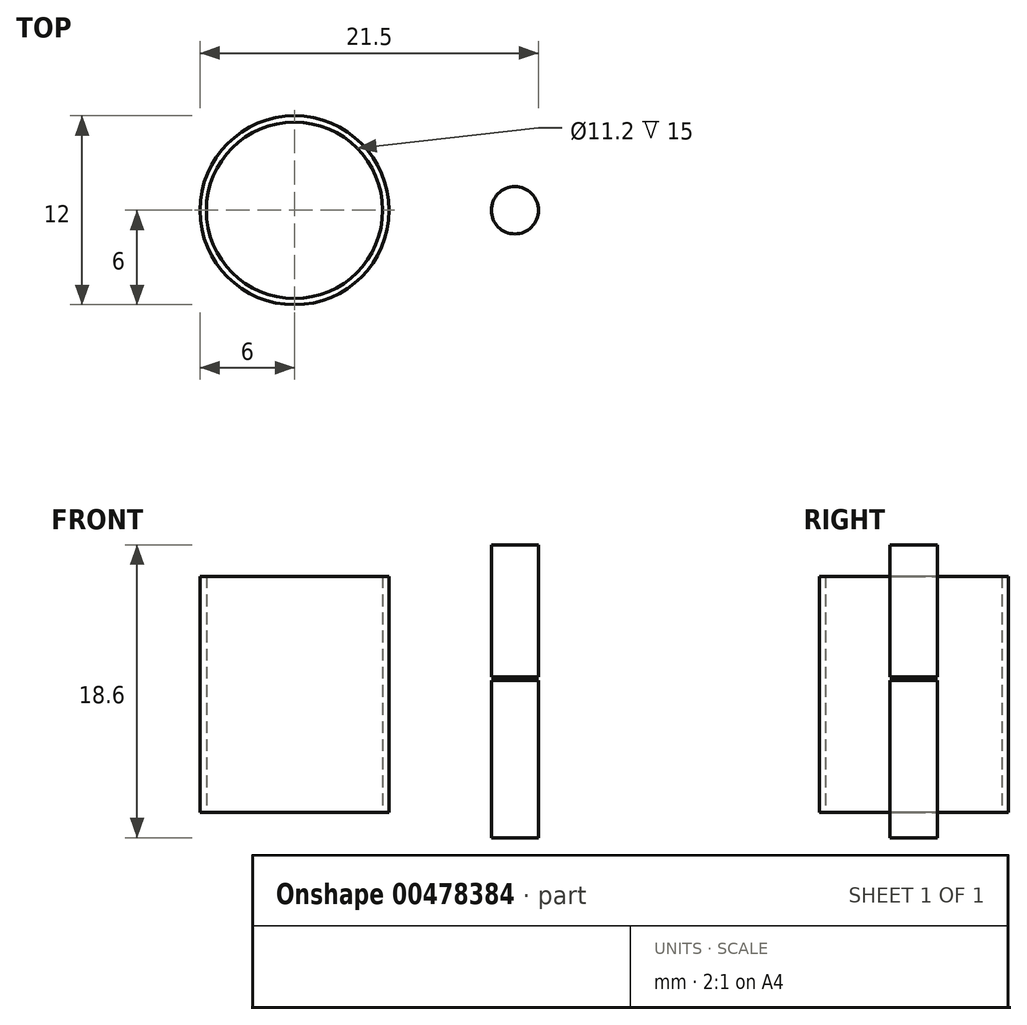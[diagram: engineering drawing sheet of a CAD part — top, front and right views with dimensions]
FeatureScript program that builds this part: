
annotation { "Feature Type Name" : "Feature", "Feature Type Description" : "" }
export const myFeature = defineFeature(function(context is Context, id is Id, definition is map)
    precondition{}
    {
        {
            assignVariable(context, id + "F0", {"name" : "dMaskThick", "anyValue" : .9});
        }
        {
            assignVariable(context, id + "F1", {"name" : "outerRingHeight", "anyValue" : 10});
        }
        {
            assignVariable(context, id + "F2", {"name" : "bottomLip", "anyValue" : .5});
        }
        {
            assignVariable(context, id + "F3", {"name" : "innerSquareHeight", "anyValue" : getVariable(context, 'outerRingHeight') - getVariable(context, 'dMaskThick') - getVariable(context, 'bottomLip')});
        }
        {
            assignVariable(context, id + "F4", {"name" : "innerRingHeight", "anyValue" : 15});
        }
        {
            var Q0;
            Q0=qCreatedBy(makeId("Top.planeOp"),FACE);
            var sketch = newSketch(context, id + "F5", { "sketchPlane" : qUnion([Q0])});
            skCircle(sketch, "E0", {"center": v(0, 0) * mm, "radius": 6 * mm});
            skCircle(sketch, "E1", {"center": v(0, 0) * mm, "radius": 17 * mm});
            skCircle(sketch, "E2", {"center": v(0, 0) * mm, "radius": 8.1 * mm});
            skCircle(sketch, "E3.cCircle", {"center": v(0, 0) * mm, "radius": 15 * mm});
            skLineSegment(sketch, "E3.0", {"start": v(10.6, -10.6) * mm, "end": v(-10.6, -10.6) * mm});
            skLineSegment(sketch, "E3.1", {"start": v(-10.6, -10.6) * mm, "end": v(-10.6, 10.6) * mm});
            skLineSegment(sketch, "E3.2", {"start": v(-10.6, 10.6) * mm, "end": v(10.6, 10.6) * mm});
            skLineSegment(sketch, "E3.3", {"start": v(10.6, 10.6) * mm, "end": v(10.6, -10.6) * mm});
            skLineSegment(sketch, "E4", {"start": v(-25.02, 0) * mm, "end": v(35.29, 0) * mm, "construction": true});
            skLineSegment(sketch, "E5", {"start": v(0, 24.03) * mm, "end": v(0, -20.76) * mm, "construction": true});
            skSolve(sketch);
        }
        {
            var Q0;
            Q0=makeQuery(id+"F5.imprint","IMPRINT",FACE,{"disambiguationData":[TD([[makeQuery(id+"F5.imprint","IMPRINT",EDGE,{"derivedFrom":sQuery(id+"F5.wireOp",EDGE,"E1")}),1.0]])]});
            var Q1;
            {var subQ0=sQuery(id+"F5.wireOp",EDGE,"E3.2");Q1=makeQuery(id+"F5.imprint","IMPRINT",FACE,{"disambiguationData":[TD([[makeQuery(id+"F5.imprint","IMPRINT",EDGE,{"derivedFrom":subQ0}),1.0]])]});}
            var Q2;
            {var subQ0=sQuery(id+"F5.wireOp",EDGE,"E3.1");Q2=makeQuery(id+"F5.imprint","IMPRINT",FACE,{"disambiguationData":[TD([[makeQuery(id+"F5.imprint","IMPRINT",EDGE,{"derivedFrom":subQ0}),1.0]])]});}
            var Q3;
            {var subQ0=sQuery(id+"F5.wireOp",EDGE,"E3.3");Q3=makeQuery(id+"F5.imprint","IMPRINT",FACE,{"disambiguationData":[TD([[makeQuery(id+"F5.imprint","IMPRINT",EDGE,{"derivedFrom":subQ0}),1.0]])]});}
            var Q4;
            {var subQ0=sQuery(id+"F5.wireOp",EDGE,"E3.0");Q4=makeQuery(id+"F5.imprint","IMPRINT",FACE,{"disambiguationData":[TD([[makeQuery(id+"F5.imprint","IMPRINT",EDGE,{"derivedFrom":subQ0}),1.0]])]});}
            var Q5;
            Q5=makeQuery(id+"F5.imprint","IMPRINT",FACE,{"disambiguationData":[TD([[makeQuery(id+"F5.imprint","IMPRINT",EDGE,{"derivedFrom":sQuery(id+"F5.wireOp",EDGE,"E2")}),-1.0]])]});
            var Q6;
            Q6=makeQuery(id+"F5.imprint","IMPRINT",FACE,{"disambiguationData":[TD([[makeQuery(id+"F5.imprint","IMPRINT",EDGE,{"derivedFrom":sQuery(id+"F5.wireOp",EDGE,"E0")}),-1.0]])]});
            extrude(context, id + "F6", {"entities" : qUnion([Q0, Q1, Q2, Q3, Q4, Q5, Q6]), "depth" : (getVariable(context, 'bottomLip')) * mm});
        }
        {
            var Q0;
            Q0=makeQuery(id+"F5.imprint","IMPRINT",FACE,{"disambiguationData":[TD([[makeQuery(id+"F5.imprint","IMPRINT",EDGE,{"derivedFrom":sQuery(id+"F5.wireOp",EDGE,"E1")}),1.0]])]});
            var Q1;
            {var subQ0=sQuery(id+"F5.wireOp",EDGE,"E3.1");Q1=makeQuery(id+"F5.imprint","IMPRINT",FACE,{"disambiguationData":[TD([[makeQuery(id+"F5.imprint","IMPRINT",EDGE,{"derivedFrom":subQ0}),1.0]])]});}
            var Q2;
            {var subQ0=sQuery(id+"F5.wireOp",EDGE,"E3.2");Q2=makeQuery(id+"F5.imprint","IMPRINT",FACE,{"disambiguationData":[TD([[makeQuery(id+"F5.imprint","IMPRINT",EDGE,{"derivedFrom":subQ0}),1.0]])]});}
            var Q3;
            {var subQ0=sQuery(id+"F5.wireOp",EDGE,"E3.3");Q3=makeQuery(id+"F5.imprint","IMPRINT",FACE,{"disambiguationData":[TD([[makeQuery(id+"F5.imprint","IMPRINT",EDGE,{"derivedFrom":subQ0}),1.0]])]});}
            var Q4;
            {var subQ0=sQuery(id+"F5.wireOp",EDGE,"E3.0");Q4=makeQuery(id+"F5.imprint","IMPRINT",FACE,{"disambiguationData":[TD([[makeQuery(id+"F5.imprint","IMPRINT",EDGE,{"derivedFrom":subQ0}),1.0]])]});}
            extrude(context, id + "F7", {"entities" : qUnion([Q0, Q1, Q2, Q3, Q4]), "operationType" : NewBodyOperationType.ADD, "depth" : getVariable(context, 'outerRingHeight') * mm});
        }
        {
            var Q0;
            Q0=makeQuery(id+"F6.opExtrude","CAP_FACE",FACE,{"disambiguationData":[OSD([sQuery(id+"F5.wireOp",EDGE,"E0"),sQuery(id+"F5.wireOp",EDGE,"E1")])],"isStart":false});
            var sketch = newSketch(context, id + "F8", { "sketchPlane" : qUnion([Q0])});
            skCircle(sketch, "E6.cCircle", {"center": v(0, 0) * mm, "radius": 14.7 * mm, "construction": true});
            skLineSegment(sketch, "E6.0", {"start": v(10.4, 10.4) * mm, "end": v(10.4, -10.4) * mm});
            skLineSegment(sketch, "E6.1", {"start": v(10.4, -10.4) * mm, "end": v(-10.4, -10.4) * mm});
            skLineSegment(sketch, "E6.2", {"start": v(-10.4, -10.4) * mm, "end": v(-10.4, 10.4) * mm});
            skLineSegment(sketch, "E6.3", {"start": v(-10.4, 10.4) * mm, "end": v(10.4, 10.4) * mm});
            skLineSegment(sketch, "E7", {"start": v(-3.27, 10.4) * mm, "end": v(-3.27, -10.4) * mm});
            skLineSegment(sketch, "E8", {"start": v(-1.77, 10.4) * mm, "end": v(-1.77, -10.4) * mm});
            skSolve(sketch);
        }
        {
            var Q0;
            Q0=makeQuery(id+"F8.imprint","IMPRINT",FACE,{"disambiguationData":[TD([[makeQuery(id+"F8.imprint","IMPRINT",EDGE,{"derivedFrom":sQuery(id+"F8.wireOp",EDGE,"n2eiUsH8-K44O-pwdb-X9DC-F9IxE2vRVmvv.bottom")}),-1.0]])]});
            var Q1;
            Q1=makeQuery(id+"F8.imprint","IMPRINT",FACE,{"disambiguationData":[TD([[makeQuery(id+"F8.imprint","IMPRINT",EDGE,{"derivedFrom":sQuery(id+"F8.wireOp",EDGE,"E6.0")}),-1.0]])]});
            extrude(context, id + "F9", {"entities" : qUnion([Q0, Q1]), "depth" : (getVariable(context, 'dMaskThick')) * mm});
        }
        {
            var Q0;
            Q0=makeQuery(id+"F9.opExtrude","CAP_FACE",FACE,{"disambiguationData":[OSD([sQuery(id+"F8.wireOp",EDGE,"E6.0"),sQuery(id+"F8.wireOp",EDGE,"E6.1"),sQuery(id+"F8.wireOp",EDGE,"E6.2"),sQuery(id+"F8.wireOp",EDGE,"E6.3"),sQuery(id+"F8.wireOp",EDGE,"n2eiUsH8-K44O-pwdb-X9DC-F9IxE2vRVmvv.bottom"),sQuery(id+"F8.wireOp",EDGE,"n2eiUsH8-K44O-pwdb-X9DC-F9IxE2vRVmvv.top"),sQuery(id+"F8.wireOp",EDGE,"n2eiUsH8-K44O-pwdb-X9DC-F9IxE2vRVmvv.left"),sQuery(id+"F8.wireOp",EDGE,"n2eiUsH8-K44O-pwdb-X9DC-F9IxE2vRVmvv.right")])],"isStart":false});
            var sketch = newSketch(context, id + "F10", { "sketchPlane" : qUnion([Q0])});
            skCircle(sketch, "E9.cCircle", {"center": v(0, 0) * mm, "radius": 14.4 * mm, "construction": true});
            skLineSegment(sketch, "E9.0", {"start": v(10.18, 10.18) * mm, "end": v(10.18, -10.18) * mm});
            skLineSegment(sketch, "E9.1", {"start": v(10.18, -10.18) * mm, "end": v(-10.18, -10.18) * mm});
            skLineSegment(sketch, "E9.2", {"start": v(-10.18, -10.18) * mm, "end": v(-10.18, 10.18) * mm});
            skLineSegment(sketch, "E9.3", {"start": v(-10.18, 10.18) * mm, "end": v(10.18, 10.18) * mm});
            skCircle(sketch, "E10", {"center": v(0, 0) * mm, "radius": 8.1 * mm});
            skSolve(sketch);
        }
        {
            var Q0;
            Q0=qSketchRegion(id+"F10",true);
            extrude(context, id + "F11", {"entities" : qUnion([Q0]), "depth" : (getVariable(context, 'innerSquareHeight')) * mm});
        }
        {
            var Q0;
            Q0=qCreatedBy(makeId("Front.planeOp"),FACE);
            var sketch = newSketch(context, id + "F12", { "sketchPlane" : qUnion([Q0])});
            skCircle(sketch, "E11", {"center": v(8.5, 4) * mm, "radius": 1.1 * mm});
            skLineSegment(sketch, "E12", {"start": v(0, 23.51) * mm, "end": v(0, 0) * mm, "construction": true});
            skCircle(sketch, "E13", {"center": v(8.5, 7.44) * mm, "radius": 1.1 * mm});
            skCircle(sketch, "E14", {"center": v(8.5, 7.44) * mm, "radius": 1 * mm});
            skCircle(sketch, "E15", {"center": v(8.5, 4) * mm, "radius": 1 * mm});
            skSolve(sketch);
        }
        {
            var Q0;
            Q0=makeQuery(id+"F12.imprint","IMPRINT",FACE,{"disambiguationData":[TD([[makeQuery(id+"F12.imprint","IMPRINT",EDGE,{"derivedFrom":sQuery(id+"F12.wireOp",EDGE,"E14")}),1.0]])]});
            var Q1;
            Q1=makeQuery(id+"F12.imprint","IMPRINT",FACE,{"disambiguationData":[TD([[makeQuery(id+"F12.imprint","IMPRINT",EDGE,{"derivedFrom":sQuery(id+"F12.wireOp",EDGE,"E13")}),1.0]])]});
            var Q2;
            Q2=makeQuery(id+"F12.imprint","IMPRINT",FACE,{"disambiguationData":[TD([[makeQuery(id+"F12.imprint","IMPRINT",EDGE,{"derivedFrom":sQuery(id+"F12.wireOp",EDGE,"E15")}),1.0]])]});
            var Q3;
            Q3=makeQuery(id+"F12.imprint","IMPRINT",FACE,{"disambiguationData":[TD([[makeQuery(id+"F12.imprint","IMPRINT",EDGE,{"derivedFrom":sQuery(id+"F12.wireOp",EDGE,"E11")}),1.0]])]});
            var Q4;
            Q4=sQuery(id+"F12.wireOp",EDGE,"E12");
            revolve(context, id + "F13", {"operationType" : NewBodyOperationType.REMOVE, "entities" : qUnion([Q0, Q1, Q2, Q3]), "axis" : qUnion([Q4]), "revolveType" : RevolveType.FULL, "oppositeDirection" : true});
        }
        {
            var Q0;
            Q0=qCreatedBy(makeId("Front.planeOp"),FACE);
            var sketch = newSketch(context, id + "F14", { "sketchPlane" : qUnion([Q0])});
            skLineSegment(sketch, "E16", {"start": v(0, -4.37) * mm, "end": v(0, 15.91) * mm, "construction": true});
            skLineSegment(sketch, "E17", {"start": v(-23.99, 0) * mm, "end": v(22.47, 0) * mm, "construction": true});
            skLineSegment(sketch, "E18.bottom", {"start": v(5.6, 16.6) * mm, "end": v(7.6, 16.6) * mm});
            skLineSegment(sketch, "E18.top", {"start": v(5.6, 1.6) * mm, "end": v(7.6, 1.6) * mm});
            skLineSegment(sketch, "E18.left", {"start": v(5.6, 16.6) * mm, "end": v(5.6, 1.6) * mm});
            skLineSegment(sketch, "E18.right", {"start": v(7.6, 16.6) * mm, "end": v(7.6, 1.6) * mm});
            skSolve(sketch);
        }
        {
            var Q0;
            Q0=makeQuery(id+"F14.imprint","IMPRINT",FACE,{"disambiguationData":[TD([[makeQuery(id+"F14.imprint","IMPRINT",EDGE,{"derivedFrom":sQuery(id+"F14.wireOp",EDGE,"E18.bottom")}),-1.0]])]});
            var Q1;
            Q1=sQuery(id+"F14.wireOp",EDGE,"E16");
            revolve(context, id + "F15", {"entities" : qUnion([Q0]), "axis" : qUnion([Q1]), "revolveType" : RevolveType.FULL});
        }
        {
            var Q0;
            Q0=makeQuery(id+"F12.imprint","IMPRINT",FACE,{"disambiguationData":[TD([[makeQuery(id+"F12.imprint","IMPRINT",EDGE,{"derivedFrom":sQuery(id+"F12.wireOp",EDGE,"E14")}),1.0]])]});
            var Q1;
            Q1=makeQuery(id+"F12.imprint","IMPRINT",FACE,{"disambiguationData":[TD([[makeQuery(id+"F12.imprint","IMPRINT",EDGE,{"derivedFrom":sQuery(id+"F12.wireOp",EDGE,"E15")}),1.0]])]});
            var Q2;
            Q2=sQuery(id+"F12.wireOp",EDGE,"E12");
            revolve(context, id + "F16", {"entities" : qUnion([Q0, Q1]), "axis" : qUnion([Q2]), "revolveType" : RevolveType.FULL});
        }
        {
            var Q0;
            Q0=qCreatedBy(makeId("Top.planeOp"),FACE);
            cPlane(context, id + "F17", {"entities" : qUnion([Q0]), "cplaneType" : CPlaneType.OFFSET, "offset" : 16.6 * mm, "width" : 150 * mm, "height" : 150 * mm});
        }
        {
            var Q0;
            Q0=qCreatedBy(id+"F17.planeOp",FACE);
            var sketch = newSketch(context, id + "F18", { "sketchPlane" : qUnion([Q0])});
            skCircle(sketch, "E19", {"center": v(0, 0) * mm, "radius": 6 * mm});
            skCircle(sketch, "E20", {"center": v(0, 0) * mm, "radius": 17 * mm});
            skCircle(sketch, "E21", {"center": v(0, 0) * mm, "radius": 8.2 * mm});
            skCircle(sketch, "E22.cCircle", {"center": v(0, 0) * mm, "radius": 15 * mm});
            skLineSegment(sketch, "E22.0", {"start": v(10.6, -10.6) * mm, "end": v(-10.6, -10.6) * mm});
            skLineSegment(sketch, "E22.1", {"start": v(-10.6, -10.6) * mm, "end": v(-10.6, 10.6) * mm});
            skLineSegment(sketch, "E22.2", {"start": v(-10.6, 10.6) * mm, "end": v(10.6, 10.6) * mm});
            skLineSegment(sketch, "E22.3", {"start": v(10.6, 10.6) * mm, "end": v(10.6, -10.6) * mm});
            skLineSegment(sketch, "E23", {"start": v(0, 24.03) * mm, "end": v(0, -20.76) * mm, "construction": true});
            skSolve(sketch);
        }
        {
            var Q0;
            {var subQ0=sQuery(id+"F18.wireOp",EDGE,"E22.2");Q0=makeQuery(id+"F18.imprint","IMPRINT",FACE,{"disambiguationData":[TD([[makeQuery(id+"F18.imprint","IMPRINT",EDGE,{"derivedFrom":subQ0}),1.0]])]});}
            var Q1;
            Q1=makeQuery(id+"F18.imprint","IMPRINT",FACE,{"disambiguationData":[TD([[makeQuery(id+"F18.imprint","IMPRINT",EDGE,{"derivedFrom":sQuery(id+"F18.wireOp",EDGE,"E21")}),-1.0]])]});
            var Q2;
            {var subQ0=sQuery(id+"F18.wireOp",EDGE,"E22.1");Q2=makeQuery(id+"F18.imprint","IMPRINT",FACE,{"disambiguationData":[TD([[makeQuery(id+"F18.imprint","IMPRINT",EDGE,{"derivedFrom":subQ0}),1.0]])]});}
            var Q3;
            {var subQ0=sQuery(id+"F18.wireOp",EDGE,"E22.0");Q3=makeQuery(id+"F18.imprint","IMPRINT",FACE,{"disambiguationData":[TD([[makeQuery(id+"F18.imprint","IMPRINT",EDGE,{"derivedFrom":subQ0}),1.0]])]});}
            var Q4;
            {var subQ0=sQuery(id+"F18.wireOp",EDGE,"E22.3");Q4=makeQuery(id+"F18.imprint","IMPRINT",FACE,{"disambiguationData":[TD([[makeQuery(id+"F18.imprint","IMPRINT",EDGE,{"derivedFrom":subQ0}),1.0]])]});}
            var Q5;
            Q5=makeQuery(id+"F18.imprint","IMPRINT",FACE,{"disambiguationData":[TD([[makeQuery(id+"F18.imprint","IMPRINT",EDGE,{"derivedFrom":sQuery(id+"F18.wireOp",EDGE,"E20")}),1.0]])]});
            var Q6;
            Q6=makeQuery(id+"F18.imprint","IMPRINT",FACE,{"disambiguationData":[TD([[makeQuery(id+"F18.imprint","IMPRINT",EDGE,{"derivedFrom":sQuery(id+"F18.wireOp",EDGE,"E19")}),-1.0]])]});
            extrude(context, id + "F19", {"entities" : qUnion([Q0, Q1, Q2, Q3, Q4, Q5, Q6]), "depth" : 2 * mm});
        }
        {
            var Q0;
            Q0=makeQuery(id+"F18.imprint","IMPRINT",FACE,{"disambiguationData":[TD([[makeQuery(id+"F18.imprint","IMPRINT",EDGE,{"derivedFrom":sQuery(id+"F18.wireOp",EDGE,"E20")}),1.0]])]});
            var Q1;
            {var subQ0=sQuery(id+"F18.wireOp",EDGE,"E22.0");Q1=makeQuery(id+"F18.imprint","IMPRINT",FACE,{"disambiguationData":[TD([[makeQuery(id+"F18.imprint","IMPRINT",EDGE,{"derivedFrom":subQ0}),1.0]])]});}
            var Q2;
            {var subQ0=sQuery(id+"F18.wireOp",EDGE,"E22.1");Q2=makeQuery(id+"F18.imprint","IMPRINT",FACE,{"disambiguationData":[TD([[makeQuery(id+"F18.imprint","IMPRINT",EDGE,{"derivedFrom":subQ0}),1.0]])]});}
            var Q3;
            {var subQ0=sQuery(id+"F18.wireOp",EDGE,"E22.3");Q3=makeQuery(id+"F18.imprint","IMPRINT",FACE,{"disambiguationData":[TD([[makeQuery(id+"F18.imprint","IMPRINT",EDGE,{"derivedFrom":subQ0}),1.0]])]});}
            var Q4;
            {var subQ0=sQuery(id+"F18.wireOp",EDGE,"E22.2");Q4=makeQuery(id+"F18.imprint","IMPRINT",FACE,{"disambiguationData":[TD([[makeQuery(id+"F18.imprint","IMPRINT",EDGE,{"derivedFrom":subQ0}),1.0]])]});}
            extrude(context, id + "F20", {"entities" : qUnion([Q0, Q1, Q2, Q3, Q4]), "operationType" : NewBodyOperationType.ADD, "oppositeDirection" : true, "depth" : (getVariable(context, 'innerRingHeight') - getVariable(context, 'outerRingHeight') + getVariable(context, 'bottomLip') + getVariable(context, 'dMaskThick')) * mm});
        }
        {
            var Q0;
            Q0=makeQuery(id+"F19.opExtrude","CAP_FACE",FACE,{"disambiguationData":[OSD([sQuery(id+"F18.wireOp",EDGE,"E19"),sQuery(id+"F18.wireOp",EDGE,"E20")])],"isStart":false});
            var sketch = newSketch(context, id + "F21", { "sketchPlane" : qUnion([Q0])});
            skCircle(sketch, "E24", {"center": v(-14, 0) * mm, "radius": 1.5 * mm});
            skLineSegment(sketch, "E25", {"start": v(0, 21.2) * mm, "end": v(0, -23.2) * mm, "construction": true});
            skCircle(sketch, "E26.MirrorC", {"center": v(14, 0) * mm, "radius": 1.5 * mm});
            skSolve(sketch);
        }
        {
            var Q0;
            Q0=makeQuery(id+"F21.imprint","IMPRINT",FACE,{"disambiguationData":[TD([[makeQuery(id+"F21.imprint","IMPRINT",EDGE,{"derivedFrom":sQuery(id+"F21.wireOp",EDGE,"E24")}),1.0]])]});
            var Q1;
            Q1=makeQuery(id+"F21.imprint","IMPRINT",FACE,{"disambiguationData":[TD([[makeQuery(id+"F21.imprint","IMPRINT",EDGE,{"derivedFrom":sQuery(id+"F21.wireOp",EDGE,"E26.MirrorC")}),-1.0]])]});
            var Q2;
            Q2=makeQuery(id+"F6.opExtrude","CAP_FACE",FACE,{"disambiguationData":[OSD([sQuery(id+"F5.wireOp",EDGE,"E0"),sQuery(id+"F5.wireOp",EDGE,"E1")])],"isStart":true});
            extrude(context, id + "F22", {"entities" : qUnion([Q0, Q1]), "operationType" : NewBodyOperationType.REMOVE, "endBound" : BoundingType.UP_TO_SURFACE, "oppositeDirection" : true, "endBoundEntityFace" : qUnion([Q2]), "depth" : 25 * mm});
        }
    });
